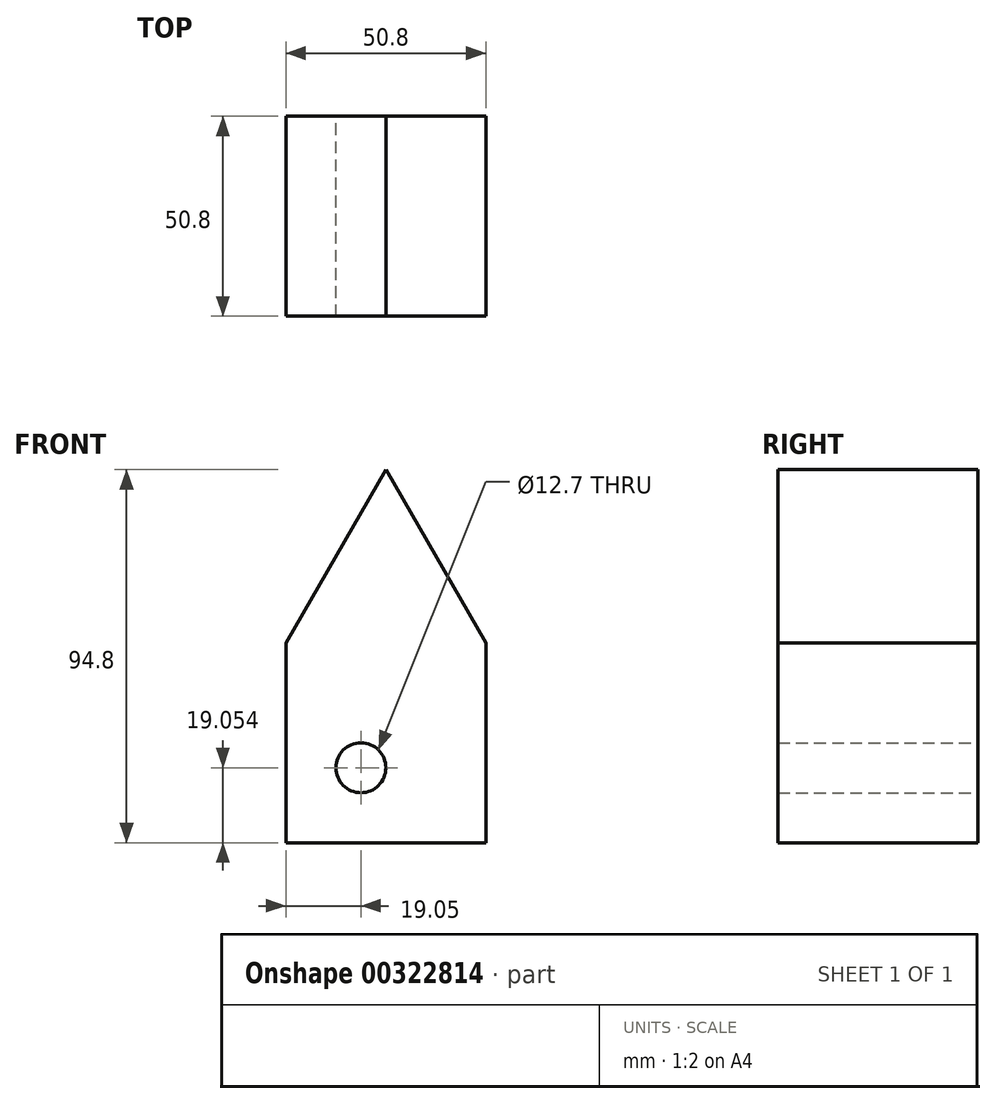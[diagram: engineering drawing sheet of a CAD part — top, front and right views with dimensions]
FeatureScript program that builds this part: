
annotation { "Feature Type Name" : "Feature", "Feature Type Description" : "" }
export const myFeature = defineFeature(function(context is Context, id is Id, definition is map)
    precondition{}
    {
        {
            var Q0;
            Q0=qCreatedBy(makeId("Front.planeOp"),FACE);
            var sketch = newSketch(context, id + "F0", { "sketchPlane" : qUnion([Q0])});
            skLineSegment(sketch, "E0.top", {"start": v(-25.4, -34.6) * mm, "end": v(25.4, -34.6) * mm});
            skLineSegment(sketch, "E0.left", {"start": v(-25.4, 16.2) * mm, "end": v(-25.4, -34.6) * mm});
            skLineSegment(sketch, "E0.right", {"start": v(25.4, 16.2) * mm, "end": v(25.4, -34.6) * mm});
            skLineSegment(sketch, "E1", {"start": v(-25.4, 16.2) * mm, "end": v(0, 60.2) * mm});
            skLineSegment(sketch, "E2", {"start": v(25.4, 16.2) * mm, "end": v(0, 60.2) * mm});
            skCircle(sketch, "E3", {"center": v(-6.35, -15.55) * mm, "radius": 6.35 * mm});
            skSolve(sketch);
        }
        {
            var Q0;
            Q0=makeQuery(id+"F0.imprint","IMPRINT",FACE,{"disambiguationData":[TD([[makeQuery(id+"F0.imprint","IMPRINT",EDGE,{"derivedFrom":sQuery(id+"F0.wireOp",EDGE,"E0.top")}),1.0]])]});
            extrude(context, id + "F1", {"entities" : qUnion([Q0]), "depth" : 50.8 * mm});
        }
    });
